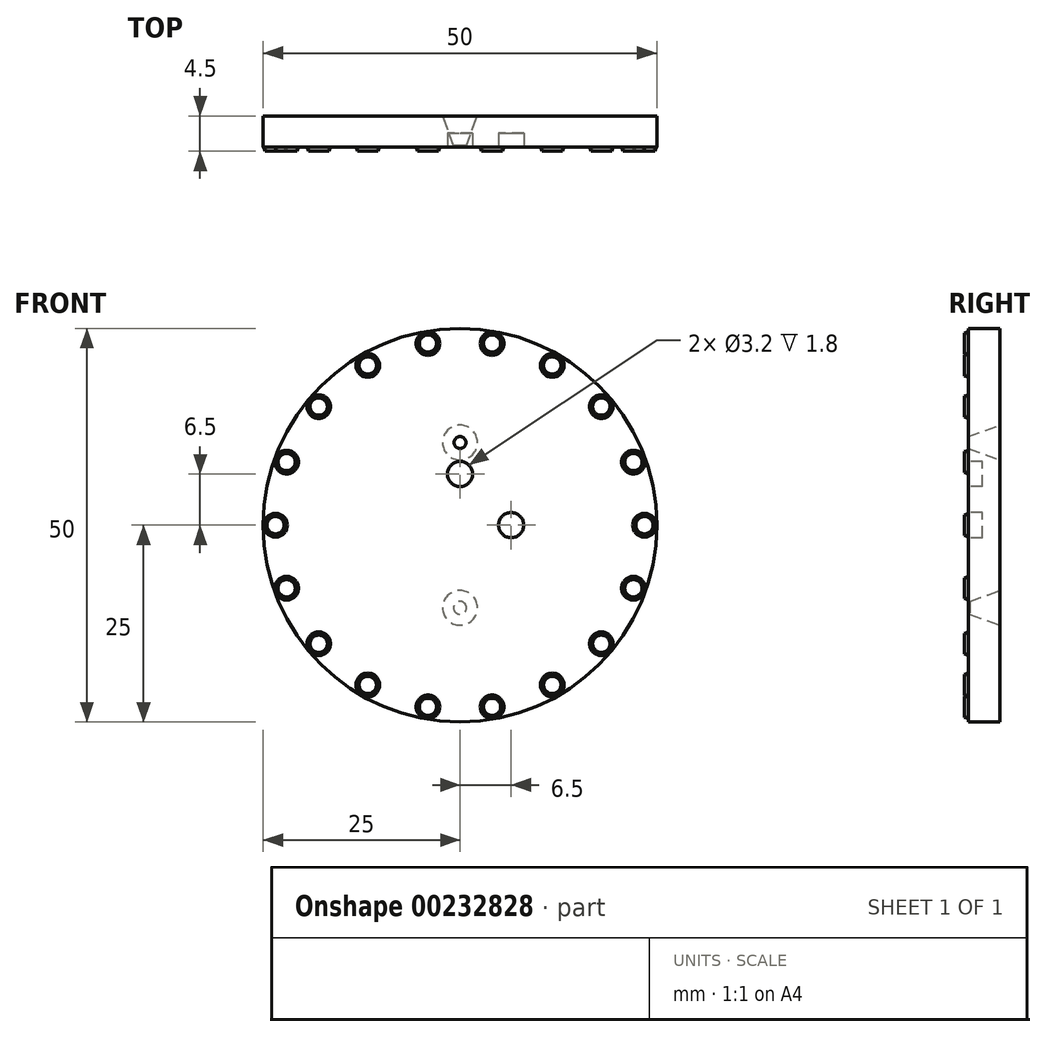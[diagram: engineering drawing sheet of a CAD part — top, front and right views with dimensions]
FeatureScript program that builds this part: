
annotation { "Feature Type Name" : "Feature", "Feature Type Description" : "" }
export const myFeature = defineFeature(function(context is Context, id is Id, definition is map)
    precondition{}
    {
        {
            var Q0;
            Q0=qCreatedBy(makeId("Front.planeOp"),FACE);
            var sketch = newSketch(context, id + "F0", { "sketchPlane" : qUnion([Q0])});
            skCircle(sketch, "E0", {"center": v(0, 0) * mm, "radius": 25 * mm});
            skSolve(sketch);
        }
        {
            var Q0;
            Q0=qSketchRegion(id+"F0",true);
            extrude(context, id + "F1", {"entities" : qUnion([Q0]), "oppositeDirection" : true, "depth" : 4 * mm});
        }
        {
            var Q0;
            Q0=qCreatedBy(makeId("Front.planeOp"),FACE);
            var sketch = newSketch(context, id + "F2", { "sketchPlane" : qUnion([Q0])});
            skCircle(sketch, "E1", {"center": v(0, 0) * mm, "radius": 15 * mm});
            skSolve(sketch);
        }
        {
            var Q0;
            Q0=makeQuery(id+"F0.imprint","IMPRINT",FACE,{"disambiguationData":[TD([[makeQuery(id+"F0.imprint","IMPRINT",EDGE,{"derivedFrom":sQuery(id+"F0.wireOp",EDGE,"E0")}),1.0]])]});
            var sketch = newSketch(context, id + "F3", { "sketchPlane" : qUnion([Q0])});
            skCircle(sketch, "E2", {"center": v(0, 6.5) * mm, "radius": 1.6 * mm});
            skCircle(sketch, "E3", {"center": v(6.5, 0) * mm, "radius": 1.6 * mm});
            skSolve(sketch);
        }
        {
            var Q0;
            Q0=makeQuery(id+"F0.imprint","IMPRINT",FACE,{"disambiguationData":[TD([[makeQuery(id+"F0.imprint","IMPRINT",EDGE,{"derivedFrom":sQuery(id+"F0.wireOp",EDGE,"E0")}),1.0]])]});
            var sketch = newSketch(context, id + "F4", { "sketchPlane" : qUnion([Q0])});
            skCircle(sketch, "E4", {"center": v(4.07, 23.08) * mm, "radius": 1.5 * mm});
            skPoint(sketch, "E5.0.midPoint", {"position": v(5.46, 22.51) * mm});
            skCircle(sketch, "E6", {"center": v(4.07, 23.08) * mm, "radius": 1.1 * mm});
            skSolve(sketch);
        }
        {
            var Q0;
            Q0=makeQuery(id+"F4.imprint","IMPRINT",FACE,{"disambiguationData":[TD([[makeQuery(id+"F4.imprint","IMPRINT",EDGE,{"derivedFrom":sQuery(id+"F4.wireOp",EDGE,"E4")}),1.0]])]});
            var Q1;
            Q1=sQuery(id+"F4.wireOp",EDGE,"E6");
            var Q2;
            Q2=sQuery(id+"F4.wireOp",EDGE,"E4");
            extrude(context, id + "F5", {"entities" : qUnion([Q0]), "surfaceEntities" : qUnion([Q1, Q2]), "depth" : 0.5 * mm, "hasDraft" : true, "draftAngle" : 20 * degree, "draftPullDirection" : true});
        }
        {
            var Q0;
            Q0=makeQuery(id+"F5.opExtrude","SWEPT_BODY",BODY,{"disambiguationData":[OSD([sQuery(id+"F4.wireOp",EDGE,"E4"),sQuery(id+"F4.wireOp",EDGE,"E6")])]});
            var Q1;
            Q1=sQuery(id+"F2.wireOp",EDGE,"E1");
            transform(context, id + "F6", {"entities" : qUnion([Q0]), "transformType" : TransformType.ROTATION, "transformAxis" : qUnion([Q1]), "angle" : 20 * degree, "makeCopy" : true});
        }
        {
            var Q0;
            Q0=makeQuery(id+"F6.opPattern","COPY",BODY,{"derivedFrom":makeQuery(id+"F5.opExtrude","SWEPT_BODY",BODY,{"disambiguationData":[OSD([sQuery(id+"F4.wireOp",EDGE,"E4"),sQuery(id+"F4.wireOp",EDGE,"E6")])]}),"instanceName":"1"});
            var Q1;
            Q1=sQuery(id+"F2.wireOp",EDGE,"E1");
            transform(context, id + "F7", {"entities" : qUnion([Q0]), "transformType" : TransformType.ROTATION, "transformAxis" : qUnion([Q1]), "angle" : 20 * degree, "makeCopy" : true});
        }
        {
            var Q0;
            Q0=makeQuery(id+"F7.opPattern","COPY",BODY,{"derivedFrom":makeQuery(id+"F6.opPattern","COPY",BODY,{"derivedFrom":makeQuery(id+"F5.opExtrude","SWEPT_BODY",BODY,{"disambiguationData":[OSD([sQuery(id+"F4.wireOp",EDGE,"E4"),sQuery(id+"F4.wireOp",EDGE,"E6")])]}),"instanceName":"1"}),"instanceName":"1"});
            var Q1;
            Q1=sQuery(id+"F2.wireOp",EDGE,"E1");
            transform(context, id + "F8", {"entities" : qUnion([Q0]), "transformType" : TransformType.ROTATION, "transformAxis" : qUnion([Q1]), "angle" : 20 * degree, "makeCopy" : true});
        }
        {
            var Q0;
            Q0=makeQuery(id+"F8.opPattern","COPY",BODY,{"derivedFrom":makeQuery(id+"F7.opPattern","COPY",BODY,{"derivedFrom":makeQuery(id+"F6.opPattern","COPY",BODY,{"derivedFrom":makeQuery(id+"F5.opExtrude","SWEPT_BODY",BODY,{"disambiguationData":[OSD([sQuery(id+"F4.wireOp",EDGE,"E4"),sQuery(id+"F4.wireOp",EDGE,"E6")])]}),"instanceName":"1"}),"instanceName":"1"}),"instanceName":"1"});
            var Q1;
            Q1=sQuery(id+"F2.wireOp",EDGE,"E1");
            transform(context, id + "F9", {"entities" : qUnion([Q0]), "transformType" : TransformType.ROTATION, "transformAxis" : qUnion([Q1]), "angle" : 20 * degree, "makeCopy" : true});
        }
        {
            var Q0;
            Q0=makeQuery(id+"F9.opPattern","COPY",BODY,{"derivedFrom":makeQuery(id+"F8.opPattern","COPY",BODY,{"derivedFrom":makeQuery(id+"F7.opPattern","COPY",BODY,{"derivedFrom":makeQuery(id+"F6.opPattern","COPY",BODY,{"derivedFrom":makeQuery(id+"F5.opExtrude","SWEPT_BODY",BODY,{"disambiguationData":[OSD([sQuery(id+"F4.wireOp",EDGE,"E4"),sQuery(id+"F4.wireOp",EDGE,"E6")])]}),"instanceName":"1"}),"instanceName":"1"}),"instanceName":"1"}),"instanceName":"1"});
            var Q1;
            Q1=sQuery(id+"F2.wireOp",EDGE,"E1");
            transform(context, id + "F10", {"entities" : qUnion([Q0]), "transformType" : TransformType.ROTATION, "transformAxis" : qUnion([Q1]), "angle" : 20 * degree, "makeCopy" : true});
        }
        {
            var Q0;
            Q0=makeQuery(id+"F5.opExtrude","SWEPT_BODY",BODY,{"disambiguationData":[OSD([sQuery(id+"F4.wireOp",EDGE,"E4"),sQuery(id+"F4.wireOp",EDGE,"E6")])]});
            var Q1;
            Q1=makeQuery(id+"F6.opPattern","COPY",BODY,{"derivedFrom":makeQuery(id+"F5.opExtrude","SWEPT_BODY",BODY,{"disambiguationData":[OSD([sQuery(id+"F4.wireOp",EDGE,"E4"),sQuery(id+"F4.wireOp",EDGE,"E6")])]}),"instanceName":"1"});
            var Q2;
            Q2=makeQuery(id+"F7.opPattern","COPY",BODY,{"derivedFrom":makeQuery(id+"F6.opPattern","COPY",BODY,{"derivedFrom":makeQuery(id+"F5.opExtrude","SWEPT_BODY",BODY,{"disambiguationData":[OSD([sQuery(id+"F4.wireOp",EDGE,"E4"),sQuery(id+"F4.wireOp",EDGE,"E6")])]}),"instanceName":"1"}),"instanceName":"1"});
            var Q3;
            Q3=makeQuery(id+"F8.opPattern","COPY",BODY,{"derivedFrom":makeQuery(id+"F7.opPattern","COPY",BODY,{"derivedFrom":makeQuery(id+"F6.opPattern","COPY",BODY,{"derivedFrom":makeQuery(id+"F5.opExtrude","SWEPT_BODY",BODY,{"disambiguationData":[OSD([sQuery(id+"F4.wireOp",EDGE,"E4"),sQuery(id+"F4.wireOp",EDGE,"E6")])]}),"instanceName":"1"}),"instanceName":"1"}),"instanceName":"1"});
            var Q4;
            Q4=makeQuery(id+"F9.opPattern","COPY",BODY,{"derivedFrom":makeQuery(id+"F8.opPattern","COPY",BODY,{"derivedFrom":makeQuery(id+"F7.opPattern","COPY",BODY,{"derivedFrom":makeQuery(id+"F6.opPattern","COPY",BODY,{"derivedFrom":makeQuery(id+"F5.opExtrude","SWEPT_BODY",BODY,{"disambiguationData":[OSD([sQuery(id+"F4.wireOp",EDGE,"E4"),sQuery(id+"F4.wireOp",EDGE,"E6")])]}),"instanceName":"1"}),"instanceName":"1"}),"instanceName":"1"}),"instanceName":"1"});
            var Q5;
            Q5=makeQuery(id+"F10.opPattern","COPY",BODY,{"derivedFrom":makeQuery(id+"F9.opPattern","COPY",BODY,{"derivedFrom":makeQuery(id+"F8.opPattern","COPY",BODY,{"derivedFrom":makeQuery(id+"F7.opPattern","COPY",BODY,{"derivedFrom":makeQuery(id+"F6.opPattern","COPY",BODY,{"derivedFrom":makeQuery(id+"F5.opExtrude","SWEPT_BODY",BODY,{"disambiguationData":[OSD([sQuery(id+"F4.wireOp",EDGE,"E4"),sQuery(id+"F4.wireOp",EDGE,"E6")])]}),"instanceName":"1"}),"instanceName":"1"}),"instanceName":"1"}),"instanceName":"1"}),"instanceName":"1"});
            var Q6;
            Q6=qCreatedBy(makeId("Top.planeOp"),FACE);
            mirror(context, id + "F11", {"entities" : qUnion([Q0, Q1, Q2, Q3, Q4, Q5]), "mirrorPlane" : qUnion([Q6])});
        }
        {
            var Q0;
            Q0=makeQuery(id+"F11.opPattern","COPY",BODY,{"derivedFrom":makeQuery(id+"F7.opPattern","COPY",BODY,{"derivedFrom":makeQuery(id+"F6.opPattern","COPY",BODY,{"derivedFrom":makeQuery(id+"F5.opExtrude","SWEPT_BODY",BODY,{"disambiguationData":[OSD([sQuery(id+"F4.wireOp",EDGE,"E4"),sQuery(id+"F4.wireOp",EDGE,"E6")])]}),"instanceName":"1"}),"instanceName":"1"}),"instanceName":"1"});
            var Q1;
            Q1=makeQuery(id+"F11.opPattern","COPY",BODY,{"derivedFrom":makeQuery(id+"F8.opPattern","COPY",BODY,{"derivedFrom":makeQuery(id+"F7.opPattern","COPY",BODY,{"derivedFrom":makeQuery(id+"F6.opPattern","COPY",BODY,{"derivedFrom":makeQuery(id+"F5.opExtrude","SWEPT_BODY",BODY,{"disambiguationData":[OSD([sQuery(id+"F4.wireOp",EDGE,"E4"),sQuery(id+"F4.wireOp",EDGE,"E6")])]}),"instanceName":"1"}),"instanceName":"1"}),"instanceName":"1"}),"instanceName":"1"});
            var Q2;
            Q2=makeQuery(id+"F11.opPattern","COPY",BODY,{"derivedFrom":makeQuery(id+"F9.opPattern","COPY",BODY,{"derivedFrom":makeQuery(id+"F8.opPattern","COPY",BODY,{"derivedFrom":makeQuery(id+"F7.opPattern","COPY",BODY,{"derivedFrom":makeQuery(id+"F6.opPattern","COPY",BODY,{"derivedFrom":makeQuery(id+"F5.opExtrude","SWEPT_BODY",BODY,{"disambiguationData":[OSD([sQuery(id+"F4.wireOp",EDGE,"E4"),sQuery(id+"F4.wireOp",EDGE,"E6")])]}),"instanceName":"1"}),"instanceName":"1"}),"instanceName":"1"}),"instanceName":"1"}),"instanceName":"1"});
            var Q3;
            Q3=makeQuery(id+"F10.opPattern","COPY",BODY,{"derivedFrom":makeQuery(id+"F9.opPattern","COPY",BODY,{"derivedFrom":makeQuery(id+"F8.opPattern","COPY",BODY,{"derivedFrom":makeQuery(id+"F7.opPattern","COPY",BODY,{"derivedFrom":makeQuery(id+"F6.opPattern","COPY",BODY,{"derivedFrom":makeQuery(id+"F5.opExtrude","SWEPT_BODY",BODY,{"disambiguationData":[OSD([sQuery(id+"F4.wireOp",EDGE,"E4"),sQuery(id+"F4.wireOp",EDGE,"E6")])]}),"instanceName":"1"}),"instanceName":"1"}),"instanceName":"1"}),"instanceName":"1"}),"instanceName":"1"});
            var Q4;
            Q4=makeQuery(id+"F9.opPattern","COPY",BODY,{"derivedFrom":makeQuery(id+"F8.opPattern","COPY",BODY,{"derivedFrom":makeQuery(id+"F7.opPattern","COPY",BODY,{"derivedFrom":makeQuery(id+"F6.opPattern","COPY",BODY,{"derivedFrom":makeQuery(id+"F5.opExtrude","SWEPT_BODY",BODY,{"disambiguationData":[OSD([sQuery(id+"F4.wireOp",EDGE,"E4"),sQuery(id+"F4.wireOp",EDGE,"E6")])]}),"instanceName":"1"}),"instanceName":"1"}),"instanceName":"1"}),"instanceName":"1"});
            var Q5;
            Q5=makeQuery(id+"F8.opPattern","COPY",BODY,{"derivedFrom":makeQuery(id+"F7.opPattern","COPY",BODY,{"derivedFrom":makeQuery(id+"F6.opPattern","COPY",BODY,{"derivedFrom":makeQuery(id+"F5.opExtrude","SWEPT_BODY",BODY,{"disambiguationData":[OSD([sQuery(id+"F4.wireOp",EDGE,"E4"),sQuery(id+"F4.wireOp",EDGE,"E6")])]}),"instanceName":"1"}),"instanceName":"1"}),"instanceName":"1"});
            var Q6;
            Q6=makeQuery(id+"F7.opPattern","COPY",BODY,{"derivedFrom":makeQuery(id+"F6.opPattern","COPY",BODY,{"derivedFrom":makeQuery(id+"F5.opExtrude","SWEPT_BODY",BODY,{"disambiguationData":[OSD([sQuery(id+"F4.wireOp",EDGE,"E4"),sQuery(id+"F4.wireOp",EDGE,"E6")])]}),"instanceName":"1"}),"instanceName":"1"});
            var Q7;
            Q7=qCreatedBy(makeId("Right.planeOp"),FACE);
            mirror(context, id + "F12", {"operationType" : NewBodyOperationType.ADD, "entities" : qUnion([Q0, Q1, Q2, Q3, Q4, Q5, Q6]), "mirrorPlane" : qUnion([Q7])});
        }
        {
            var Q0;
            Q0=makeQuery(id+"F4.imprint","IMPRINT",FACE,{"disambiguationData":[TD([[makeQuery(id+"F4.imprint","IMPRINT",EDGE,{"derivedFrom":sQuery(id+"F4.wireOp",EDGE,"E4")}),-1.0]])]});
            var sketch = newSketch(context, id + "F13", { "sketchPlane" : qUnion([Q0])});
            skCircle(sketch, "E7", {"center": v(0, 10.5) * mm, "radius": 0.75 * mm});
            skSolve(sketch);
        }
        {
            var Q0;
            Q0=makeQuery(id+"F13.imprint","IMPRINT",FACE,{"disambiguationData":[TD([[makeQuery(id+"F13.imprint","IMPRINT",EDGE,{"derivedFrom":sQuery(id+"F13.wireOp",EDGE,"E7")}),1.0]])]});
            var Q1;
            Q1=sQuery(id+"F13.wireOp",EDGE,"E7");
            extrude(context, id + "F14", {"entities" : qUnion([Q0]), "surfaceEntities" : qUnion([Q1]), "oppositeDirection" : true, "depth" : 4 * mm, "hasDraft" : true, "draftAngle" : 20 * degree});
        }
        {
            var Q0;
            Q0=makeQuery(id+"F1.opExtrude","CAP_FACE",FACE,{"disambiguationData":[OSD([sQuery(id+"F0.wireOp",EDGE,"E0")])],"isStart":false});
            var sketch = newSketch(context, id + "F15", { "sketchPlane" : qUnion([Q0])});
            skCircle(sketch, "E8", {"center": v(0, -10.5) * mm, "radius": 2.2 * mm});
            skSolve(sketch);
        }
        {
            var Q0;
            Q0=makeQuery(id+"F15.imprint","IMPRINT",FACE,{"disambiguationData":[TD([[makeQuery(id+"F15.imprint","IMPRINT",EDGE,{"derivedFrom":sQuery(id+"F15.wireOp",EDGE,"E8")}),1.0]])]});
            extrude(context, id + "F16", {"entities" : qUnion([Q0]), "operationType" : NewBodyOperationType.REMOVE, "oppositeDirection" : true, "depth" : 3.8 * mm, "hasDraft" : true, "draftAngle" : 20 * degree, "draftPullDirection" : true});
        }
        {
            var Q0;
            Q0=makeQuery(id+"F14.opExtrude","SWEPT_BODY",BODY,{"disambiguationData":[OSD([sQuery(id+"F13.wireOp",EDGE,"E7")])]});
            var Q1;
            Q1=makeQuery(id+"F1.opExtrude","SWEPT_BODY",BODY,{"disambiguationData":[OSD([sQuery(id+"F0.wireOp",EDGE,"E0")])]});
            booleanBodies(context, id + "F17", {"operationType" : BooleanOperationType.SUBTRACTION, "tools" : qUnion([Q0]), "targets" : qUnion([Q1])});
        }
        {
            var Q0;
            Q0=makeQuery(id+"F3.imprint","IMPRINT",FACE,{"disambiguationData":[TD([[makeQuery(id+"F3.imprint","IMPRINT",EDGE,{"derivedFrom":sQuery(id+"F3.wireOp",EDGE,"E3")}),1.0]])]});
            var Q1;
            Q1=makeQuery(id+"F3.imprint","IMPRINT",FACE,{"disambiguationData":[TD([[makeQuery(id+"F3.imprint","IMPRINT",EDGE,{"derivedFrom":sQuery(id+"F3.wireOp",EDGE,"E2")}),1.0]])]});
            extrude(context, id + "F18", {"entities" : qUnion([Q0, Q1]), "operationType" : NewBodyOperationType.REMOVE, "oppositeDirection" : true, "depth" : 1.8 * mm});
        }
    });
